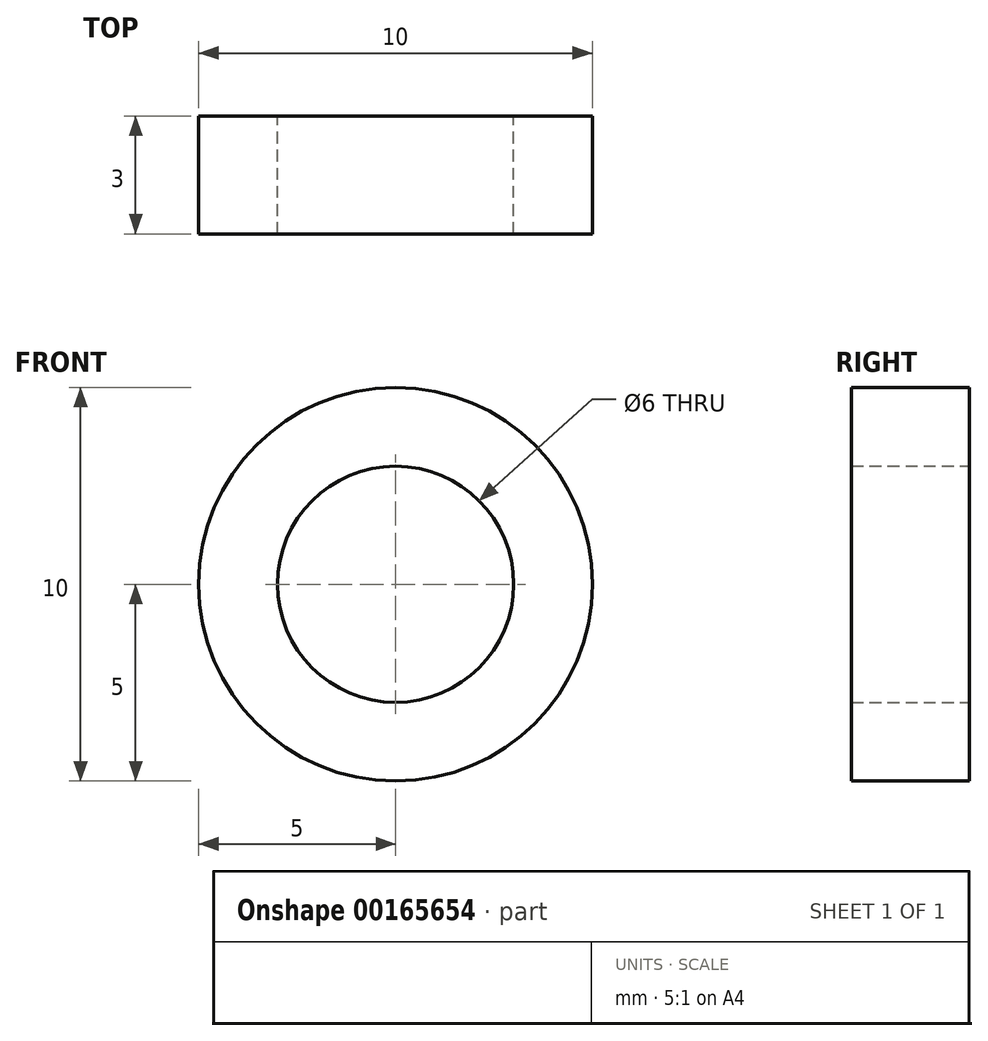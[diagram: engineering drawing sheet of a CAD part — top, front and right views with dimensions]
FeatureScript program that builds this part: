
annotation { "Feature Type Name" : "Feature", "Feature Type Description" : "" }
export const myFeature = defineFeature(function(context is Context, id is Id, definition is map)
    precondition{}
    {
        {
            var Q0;
            Q0=qCreatedBy(makeId("Front.planeOp"),FACE);
            var sketch = newSketch(context, id + "F0", { "sketchPlane" : qUnion([Q0])});
            skCircle(sketch, "E0", {"center": v(0, 0) * mm, "radius": 3 * mm});
            skCircle(sketch, "E1", {"center": v(0, 0) * mm, "radius": 5 * mm});
            skSolve(sketch);
        }
        {
            var Q0;
            Q0=makeQuery(id+"F0.imprint","IMPRINT",FACE,{"disambiguationData":[TD([[makeQuery(id+"F0.imprint","IMPRINT",EDGE,{"derivedFrom":sQuery(id+"F0.wireOp",EDGE,"E0")}),-1.0]])]});
            extrude(context, id + "F1", {"entities" : qUnion([Q0]), "depth" : 3 * mm, "offsetDistance" : 25 * mm});
        }
    });
